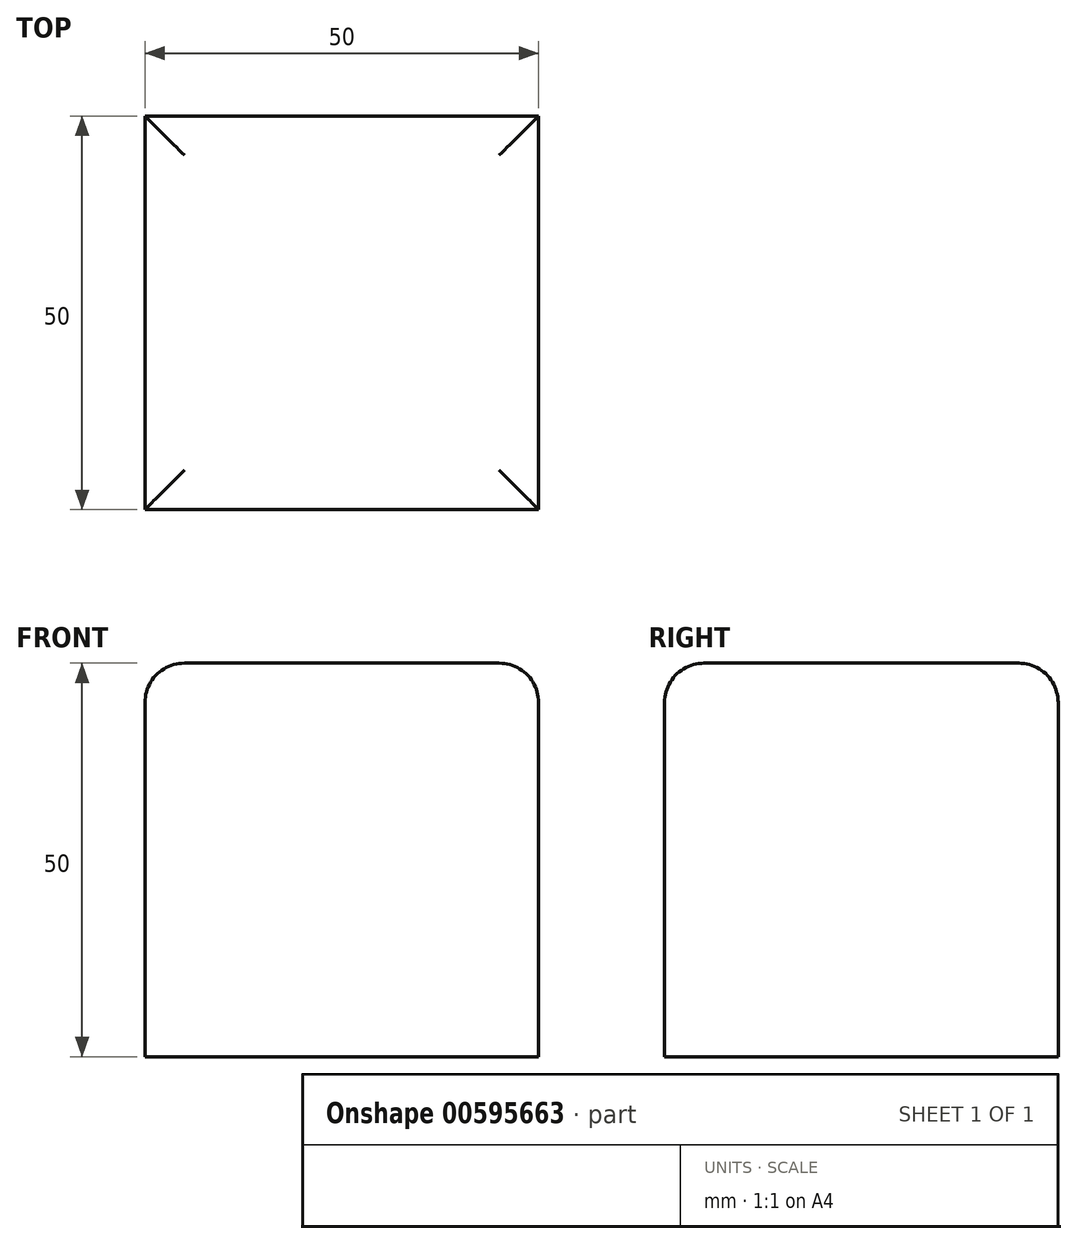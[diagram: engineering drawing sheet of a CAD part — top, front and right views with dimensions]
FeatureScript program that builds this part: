
annotation { "Feature Type Name" : "Feature", "Feature Type Description" : "" }
export const myFeature = defineFeature(function(context is Context, id is Id, definition is map)
    precondition{}
    {
        {
            var Q0;
            Q0=qCreatedBy(makeId("Front.planeOp"),FACE);
            var sketch = newSketch(context, id + "F0", { "sketchPlane" : qUnion([Q0])});
            skLineSegment(sketch, "E0.bottom", {"start": v(25, 25) * mm, "end": v(-25, 25) * mm});
            skLineSegment(sketch, "E0.top", {"start": v(25, -25) * mm, "end": v(-25, -25) * mm});
            skLineSegment(sketch, "E0.left", {"start": v(25, 25) * mm, "end": v(25, -25) * mm});
            skLineSegment(sketch, "E0.right", {"start": v(-25, 25) * mm, "end": v(-25, -25) * mm});
            skPoint(sketch, "E0.middle", {"position": v(0, 0) * mm});
            skSolve(sketch);
        }
        {
            var Q0;
            Q0 = qSketchRegion(id + "F0", true);
            extrude(context, id + "F1", {"entities" : qUnion([Q0]), "depth" : 50 * mm, "offsetDistance" : 25 * mm});
        }
        {
            var Q0;
            Q0=makeQuery(id+"F1.opExtrude","SWEPT_FACE",FACE,{"disambiguationData":[OSD([sQuery(id+"F0.wireOp",EDGE,"E0.bottom")])]});
            fillet(context, id + "F2", {"entities" : qUnion([Q0]), "radius" : 5 * mm, "tangentPropagation" : true, "allowEdgeOverflow" : false});
        }
    });
